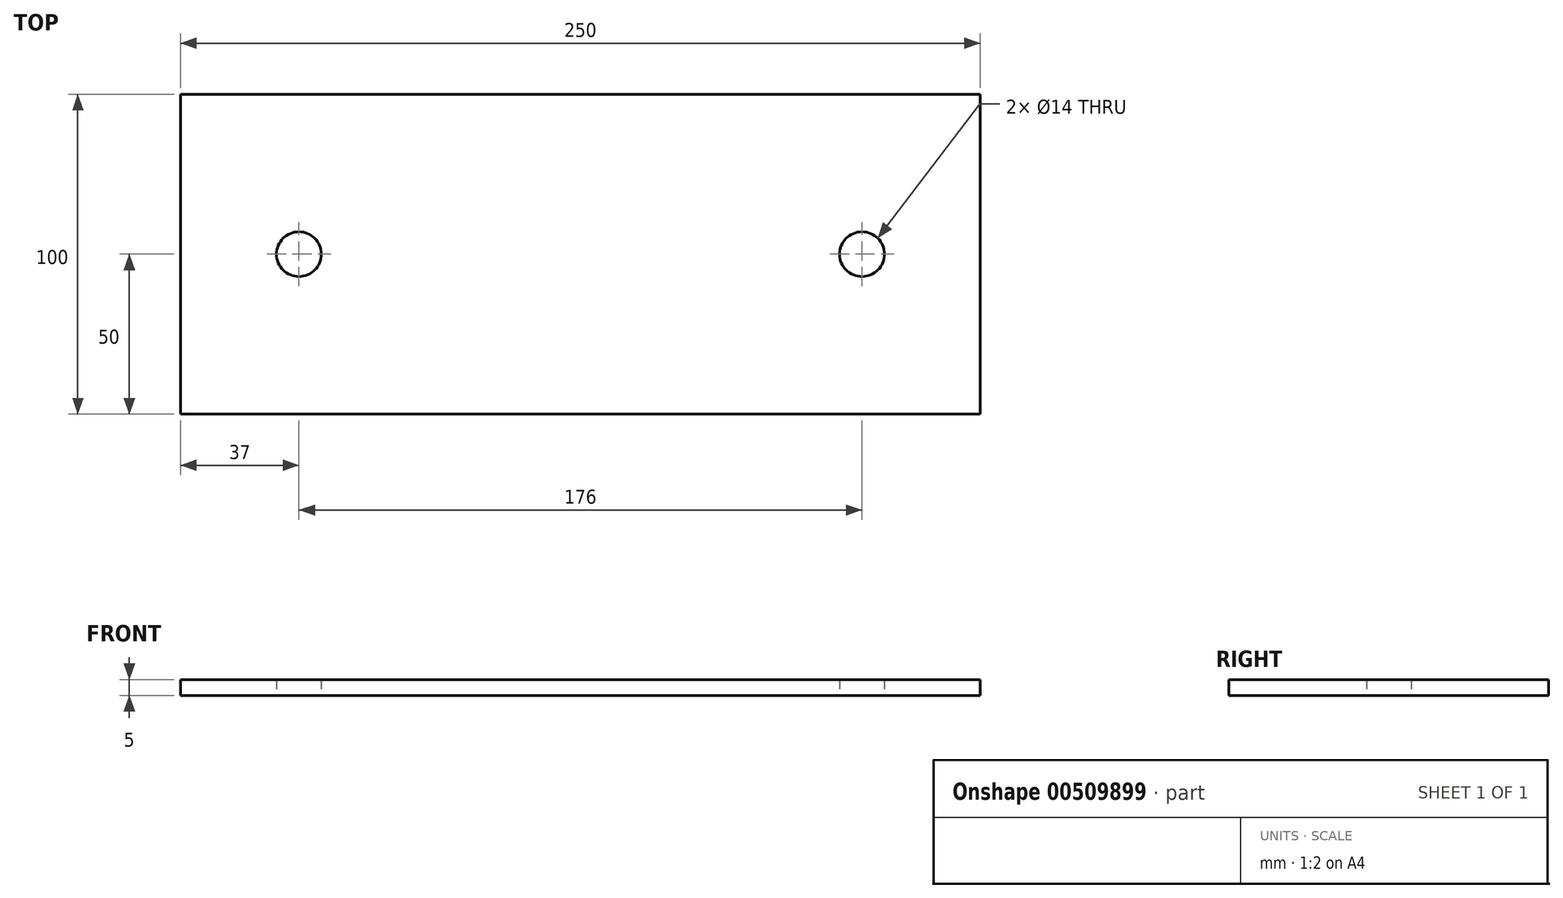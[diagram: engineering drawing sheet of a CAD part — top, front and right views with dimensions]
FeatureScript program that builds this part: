
annotation { "Feature Type Name" : "Feature", "Feature Type Description" : "" }
export const myFeature = defineFeature(function(context is Context, id is Id, definition is map)
    precondition{}
    {
        {
            var Q0;
            Q0=qCreatedBy(makeId("Top.planeOp"),FACE);
            var sketch = newSketch(context, id + "F0", { "sketchPlane" : qUnion([Q0])});
            skLineSegment(sketch, "E0.bottom", {"start": v(125, -50) * mm, "end": v(-125, -50) * mm});
            skLineSegment(sketch, "E0.top", {"start": v(125, 50) * mm, "end": v(-125, 50) * mm});
            skLineSegment(sketch, "E0.left", {"start": v(125, -50) * mm, "end": v(125, 50) * mm});
            skLineSegment(sketch, "E0.right", {"start": v(-125, -50) * mm, "end": v(-125, 50) * mm});
            skPoint(sketch, "E0.middle", {"position": v(0, 0) * mm});
            skCircle(sketch, "E1", {"center": v(88, 0) * mm, "radius": 7 * mm});
            skCircle(sketch, "E2", {"center": v(-88, 0) * mm, "radius": 7 * mm});
            skSolve(sketch);
        }
        {
            var Q0;
            Q0 = qSketchRegion(id + "F0", true);
            extrude(context, id + "F1", {"entities" : qUnion([Q0]), "depth" : 5 * mm});
        }
    });
